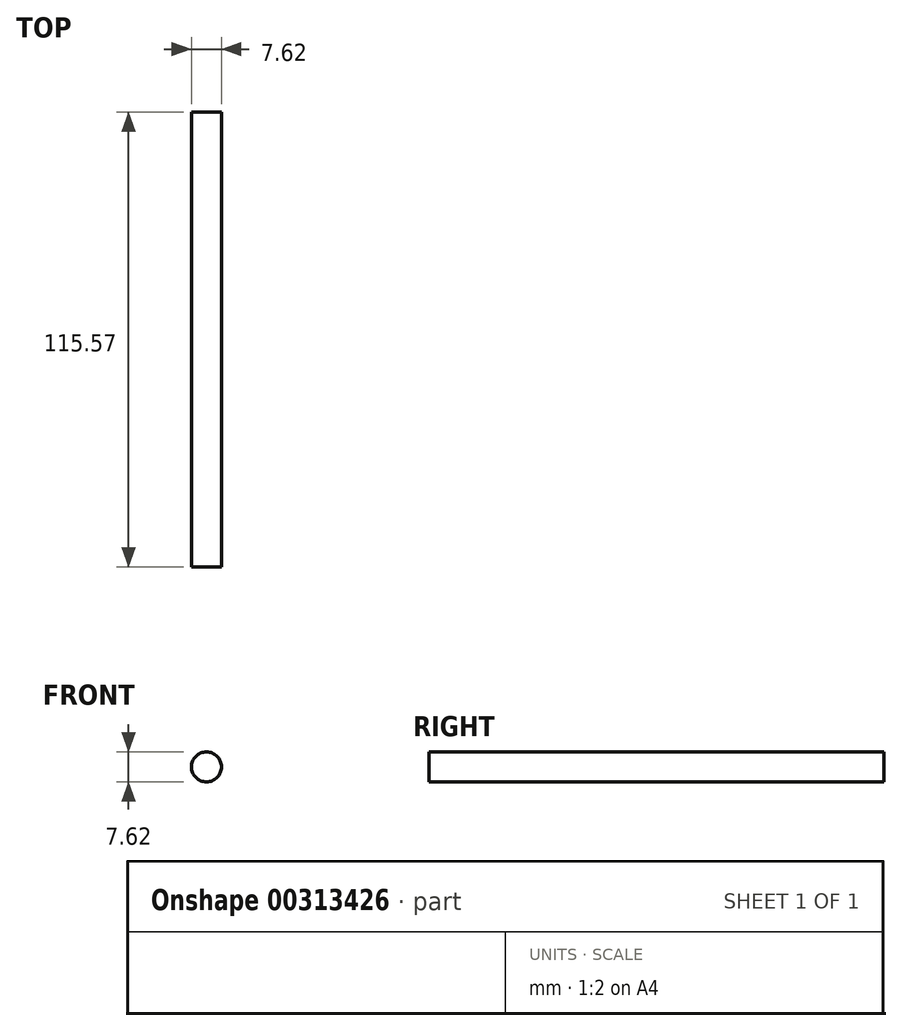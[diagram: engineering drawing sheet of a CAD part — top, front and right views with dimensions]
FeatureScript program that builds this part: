
annotation { "Feature Type Name" : "Feature", "Feature Type Description" : "" }
export const myFeature = defineFeature(function(context is Context, id is Id, definition is map)
    precondition{}
    {
        {
            var Q0;
            Q0=qCreatedBy(makeId("Front.planeOp"),FACE);
            var sketch = newSketch(context, id + "F0", { "sketchPlane" : qUnion([Q0])});
            skCircle(sketch, "E0", {"center": v(0, 0) * mm, "radius": 3.81 * mm});
            skSolve(sketch);
        }
        {
            var Q0;
            Q0 = qSketchRegion(id + "F0", true);
            extrude(context, id + "F1", {"entities" : qUnion([Q0]), "depth" : 115.57 * mm});
        }
    });
